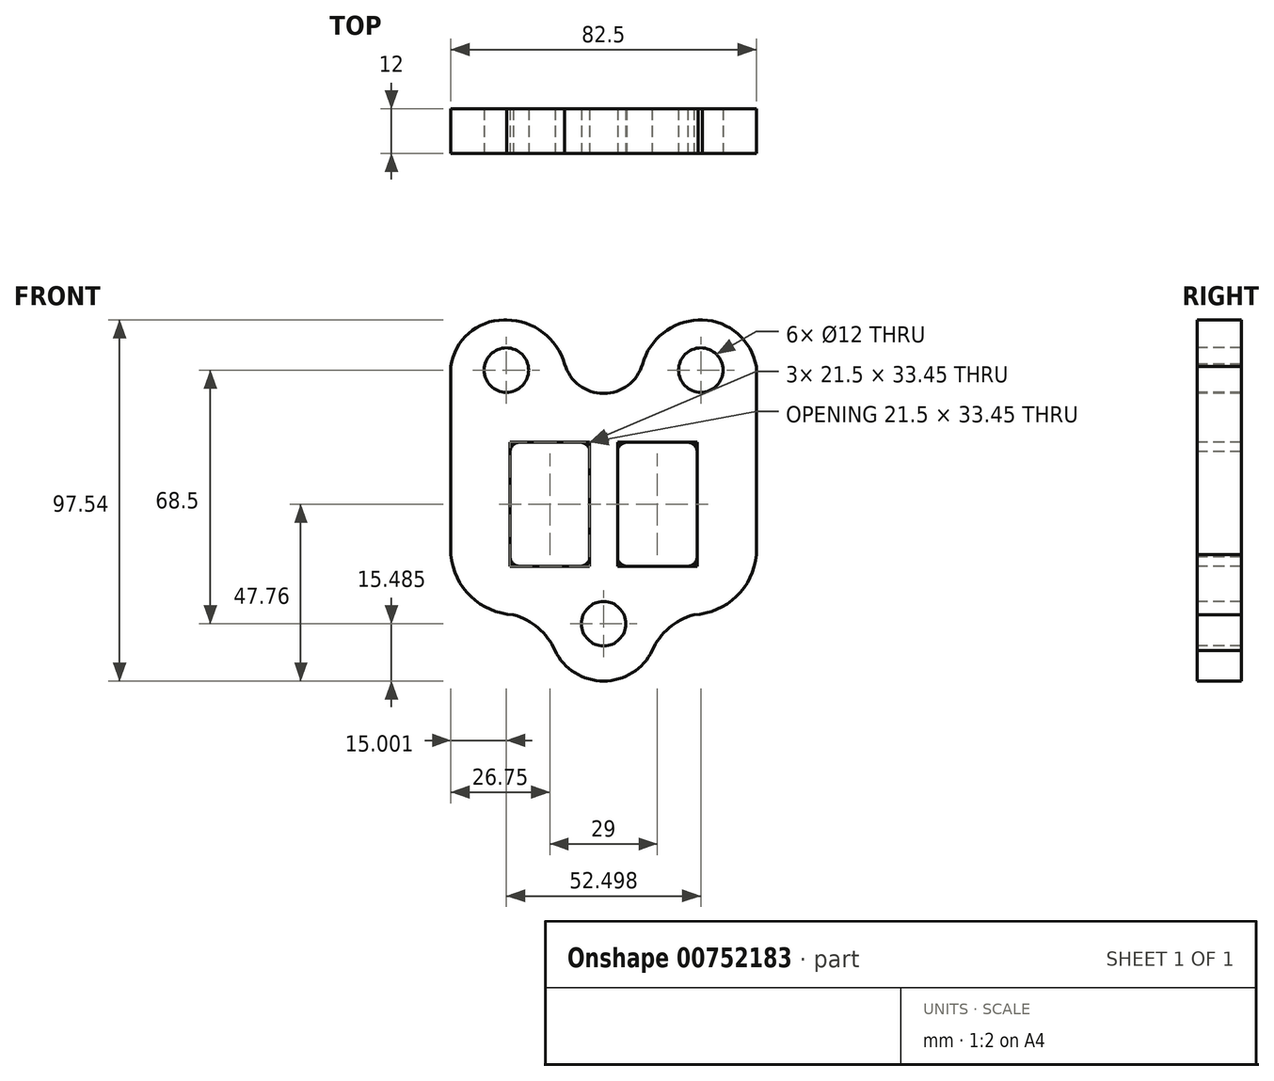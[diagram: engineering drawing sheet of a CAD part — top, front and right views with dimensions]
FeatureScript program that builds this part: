
annotation { "Feature Type Name" : "Feature", "Feature Type Description" : "" }
export const myFeature = defineFeature(function(context is Context, id is Id, definition is map)
    precondition{}
    {
        {
            var Q0;
            Q0=qCreatedBy(makeId("Front.planeOp"),FACE);
            var sketch = newSketch(context, id + "F0", { "sketchPlane" : qUnion([Q0])});
            skLineSegment(sketch, "E0.bottom", {"start": v(-41.25, 48.77) * mm, "end": v(41.25, 48.77) * mm});
            skLineSegment(sketch, "E0.top", {"start": v(-41.25, -48.77) * mm, "end": v(41.25, -48.77) * mm});
            skLineSegment(sketch, "E0.left", {"start": v(-41.25, 48.77) * mm, "end": v(-41.25, -48.77) * mm});
            skLineSegment(sketch, "E0.right", {"start": v(41.25, 48.77) * mm, "end": v(41.25, -48.77) * mm});
            skPoint(sketch, "E0.middle", {"position": v(0, 0) * mm});
            skLineSegment(sketch, "E1.bottom", {"start": v(-25.25, -17.73) * mm, "end": v(-3.75, -17.73) * mm});
            skLineSegment(sketch, "E1.top", {"start": v(-25.25, 15.72) * mm, "end": v(-3.75, 15.72) * mm});
            skLineSegment(sketch, "E1.left", {"start": v(-25.25, -17.73) * mm, "end": v(-25.25, 15.72) * mm});
            skLineSegment(sketch, "E1.right", {"start": v(-3.75, -17.73) * mm, "end": v(-3.75, 15.72) * mm});
            skLineSegment(sketch, "E2.bottom", {"start": v(3.75, -17.73) * mm, "end": v(25.25, -17.73) * mm});
            skLineSegment(sketch, "E2.top", {"start": v(3.75, 15.72) * mm, "end": v(25.25, 15.72) * mm});
            skLineSegment(sketch, "E2.left", {"start": v(3.75, -17.73) * mm, "end": v(3.75, 15.72) * mm});
            skLineSegment(sketch, "E2.right", {"start": v(25.25, -17.73) * mm, "end": v(25.25, 15.72) * mm});
            skCircle(sketch, "E3", {"center": v(-26.25, 35.22) * mm, "radius": 6 * mm});
            skCircle(sketch, "E4", {"center": v(26.25, 35.22) * mm, "radius": 6 * mm});
            skCircle(sketch, "E5", {"center": v(0, -33.28) * mm, "radius": 6 * mm});
            skSolve(sketch);
        }
        {
            var Q0;
            Q0=makeQuery(id+"F0.imprint","IMPRINT",FACE,{"disambiguationData":[TD([[makeQuery(id+"F0.imprint","IMPRINT",EDGE,{"derivedFrom":sQuery(id+"F0.wireOp",EDGE,"E0.bottom")}),-1.0]])]});
            var sketch = newSketch(context, id + "F1", { "sketchPlane" : qUnion([Q0])});
            skArc(sketch, "E6", {"start": v(-26.69, 48.77) * mm, "mid": v(-36.34, 45.2) * mm, "end": v(-41.25, 36.17) * mm});
            skArc(sketch, "E7", {"start": v(41.25, 36.17) * mm, "mid": v(36.2, 45.04) * mm, "end": v(26.69, 48.77) * mm});
            skSolve(sketch);
        }
        {
            var Q0;
            {var subQ5=sQuery(id+"F1.wireOp",EDGE,"E7");Q0=makeQuery(id+"F1.imprint","IMPRINT",FACE,{"disambiguationData":[TD([[makeQuery(id+"F1.imprint","IMPRINT",EDGE,{"derivedFrom":subQ5}),1.0]])]});}
            var sketch = newSketch(context, id + "F2", { "sketchPlane" : qUnion([Q0])});
            skArc(sketch, "E8", {"start": v(-10.48, 36.85) * mm, "mid": v(-16.56, 45.52) * mm, "end": v(-26.64, 48.77) * mm});
            skArc(sketch, "E9", {"start": v(27, 48.77) * mm, "mid": v(16.67, 45.67) * mm, "end": v(10.48, 36.85) * mm});
            skArc(sketch, "E10", {"start": v(-10.48, 36.85) * mm, "mid": v(0, 28.9) * mm, "end": v(10.48, 36.85) * mm});
            skSolve(sketch);
        }
        {
            var Q0;
            {var subQ16=sQuery(id+"F2.wireOp",EDGE,"E10");Q0=makeQuery(id+"F2.imprint","IMPRINT",FACE,{"disambiguationData":[TD([[makeQuery(id+"F2.imprint","IMPRINT",EDGE,{"derivedFrom":subQ16}),-1.0]])]});}
            var sketch = newSketch(context, id + "F3", { "sketchPlane" : qUnion([Q0])});
            skArc(sketch, "E11", {"start": v(-13.14, -40.5) * mm, "mid": v(0, -48.76) * mm, "end": v(13.14, -40.5) * mm});
            skArc(sketch, "E12", {"start": v(24.34, -30.82) * mm, "mid": v(35.87, -25.92) * mm, "end": v(41.25, -14.6) * mm});
            skArc(sketch, "E13", {"start": v(-41.25, -14.6) * mm, "mid": v(-35.87, -25.92) * mm, "end": v(-24.34, -30.82) * mm});
            skArc(sketch, "E14", {"start": v(24.34, -30.82) * mm, "mid": v(17.68, -34.43) * mm, "end": v(13.14, -40.5) * mm});
            skArc(sketch, "E15", {"start": v(-13.14, -40.5) * mm, "mid": v(-17.68, -34.43) * mm, "end": v(-24.34, -30.82) * mm});
            skSolve(sketch);
        }
        {
            var Q0;
            {var subQ4=sQuery(id+"F3.wireOp",EDGE,"E12");Q0=makeQuery(id+"F3.imprint","IMPRINT",FACE,{"disambiguationData":[TD([[makeQuery(id+"F3.imprint","IMPRINT",EDGE,{"derivedFrom":subQ4}),1.0]])]});}
            var sketch = newSketch(context, id + "F4", { "sketchPlane" : qUnion([Q0])});
            skArc(sketch, "E16", {"start": v(-22.75, 15.72) * mm, "mid": v(-24.52, 14.98) * mm, "end": v(-25.25, 13.22) * mm});
            skArc(sketch, "E17", {"start": v(-3.75, 13.22) * mm, "mid": v(-4.48, 14.98) * mm, "end": v(-6.25, 15.72) * mm});
            skArc(sketch, "E18", {"start": v(-25.25, -15.23) * mm, "mid": v(-24.52, -17) * mm, "end": v(-22.75, -17.73) * mm});
            skArc(sketch, "E19", {"start": v(-6.25, -17.73) * mm, "mid": v(-4.48, -17) * mm, "end": v(-3.75, -15.23) * mm});
            skSolve(sketch);
        }
        {
            var Q0;
            Q0=makeQuery(id+"F4.imprint","IMPRINT",FACE,{"disambiguationData":[TD([[makeQuery(id+"F4.imprint","IMPRINT",EDGE,{"derivedFrom":makeQuery(id+"F3.imprint","IMPRINT",EDGE,{"derivedFrom":makeQuery(id+"F2.imprint","IMPRINT",EDGE,{"derivedFrom":makeQuery(id+"F1.imprint","IMPRINT",EDGE,{"derivedFrom":makeQuery(id+"F0.imprint","IMPRINT",EDGE,{"derivedFrom":sQuery(id+"F0.wireOp",EDGE,"E2.bottom")})})})})}),1.0]])]});
            var sketch = newSketch(context, id + "F5", { "sketchPlane" : qUnion([Q0])});
            skArc(sketch, "E20", {"start": v(6.25, 15.72) * mm, "mid": v(4.48, 14.98) * mm, "end": v(3.75, 13.22) * mm});
            skArc(sketch, "E21", {"start": v(25.25, 13.22) * mm, "mid": v(24.52, 14.98) * mm, "end": v(22.75, 15.72) * mm});
            skArc(sketch, "E22", {"start": v(3.75, -15.23) * mm, "mid": v(4.48, -17) * mm, "end": v(6.25, -17.73) * mm});
            skArc(sketch, "E23", {"start": v(22.75, -17.73) * mm, "mid": v(24.52, -17) * mm, "end": v(25.25, -15.23) * mm});
            skSolve(sketch);
        }
        {
            var Q0;
            {var subQ0=sQuery(id+"F5.wireOp",EDGE,"E21");Q0=makeQuery(id+"F5.imprint","IMPRINT",FACE,{"disambiguationData":[TD([[makeQuery(id+"F5.imprint","IMPRINT",EDGE,{"derivedFrom":subQ0}),-1.0]])]});}
            var Q1;
            {var subQ0=sQuery(id+"F4.wireOp",EDGE,"E19");Q1=makeQuery(id+"F4.imprint","IMPRINT",FACE,{"disambiguationData":[TD([[makeQuery(id+"F4.imprint","IMPRINT",EDGE,{"derivedFrom":subQ0}),-1.0]])]});}
            var Q2;
            {var subQ0=sQuery(id+"F5.wireOp",EDGE,"E20");Q2=makeQuery(id+"F5.imprint","IMPRINT",FACE,{"disambiguationData":[TD([[makeQuery(id+"F5.imprint","IMPRINT",EDGE,{"derivedFrom":subQ0}),-1.0]])]});}
            var Q3;
            {var subQ0=sQuery(id+"F4.wireOp",EDGE,"E16");Q3=makeQuery(id+"F4.imprint","IMPRINT",FACE,{"disambiguationData":[TD([[makeQuery(id+"F4.imprint","IMPRINT",EDGE,{"derivedFrom":subQ0}),-1.0]])]});}
            var Q4;
            {var subQ0=sQuery(id+"F4.wireOp",EDGE,"E17");Q4=makeQuery(id+"F4.imprint","IMPRINT",FACE,{"disambiguationData":[TD([[makeQuery(id+"F4.imprint","IMPRINT",EDGE,{"derivedFrom":subQ0}),-1.0]])]});}
            var Q5;
            {var subQ0=sQuery(id+"F4.wireOp",EDGE,"E18");Q5=makeQuery(id+"F4.imprint","IMPRINT",FACE,{"disambiguationData":[TD([[makeQuery(id+"F4.imprint","IMPRINT",EDGE,{"derivedFrom":subQ0}),-1.0]])]});}
            var Q6;
            {var subQ0=sQuery(id+"F5.wireOp",EDGE,"E23");Q6=makeQuery(id+"F5.imprint","IMPRINT",FACE,{"disambiguationData":[TD([[makeQuery(id+"F5.imprint","IMPRINT",EDGE,{"derivedFrom":subQ0}),-1.0]])]});}
            var Q7;
            {var subQ0=sQuery(id+"F5.wireOp",EDGE,"E22");Q7=makeQuery(id+"F5.imprint","IMPRINT",FACE,{"disambiguationData":[TD([[makeQuery(id+"F5.imprint","IMPRINT",EDGE,{"derivedFrom":subQ0}),-1.0]])]});}
            var Q8;
            {var subQ4=sQuery(id+"F3.wireOp",EDGE,"E12");Q8=makeQuery(id+"F3.imprint","IMPRINT",FACE,{"disambiguationData":[TD([[makeQuery(id+"F3.imprint","IMPRINT",EDGE,{"derivedFrom":subQ4}),1.0]])]});}
            var Q9;
            {var subQ15=sQuery(id+"F3.wireOp",EDGE,"E12");Q9=makeQuery(id+"F4.imprint","IMPRINT",FACE,{"disambiguationData":[TD([[makeQuery(id+"F4.imprint","IMPRINT",EDGE,{"derivedFrom":makeQuery(id+"F3.imprint","IMPRINT",EDGE,{"derivedFrom":subQ15})}),1.0]])]});}
            extrude(context, id + "F6", {"entities" : qUnion([Q0, Q1, Q2, Q3, Q4, Q5, Q6, Q7, Q8, Q9]), "oppositeDirection" : true, "depth" : 12 * mm, "offsetDistance" : 25 * mm});
        }
    });
